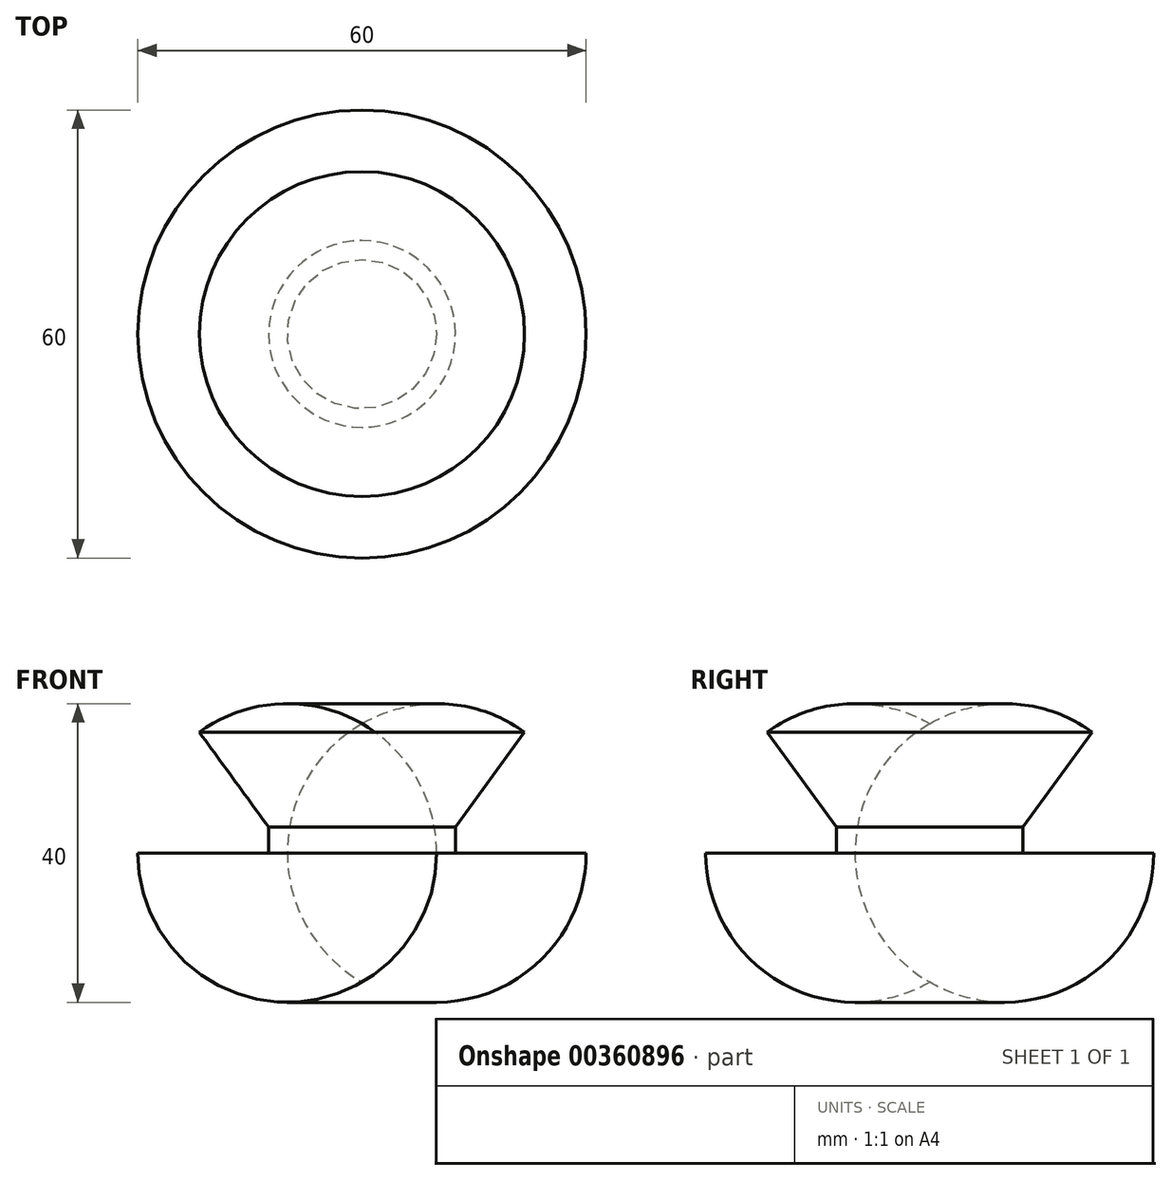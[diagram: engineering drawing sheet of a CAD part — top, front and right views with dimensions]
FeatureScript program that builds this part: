
annotation { "Feature Type Name" : "Feature", "Feature Type Description" : "" }
export const myFeature = defineFeature(function(context is Context, id is Id, definition is map)
    precondition{}
    {
        {
            var Q0;
            Q0=qCreatedBy(makeId("Front.planeOp"),FACE);
            var sketch = newSketch(context, id + "F0", { "sketchPlane" : qUnion([Q0])});
            skLineSegment(sketch, "E0", {"start": v(0, 0) * mm, "end": v(10, 0) * mm});
            skLineSegment(sketch, "E1", {"start": v(0, 0) * mm, "end": v(0, 20) * mm});
            skLineSegment(sketch, "E2", {"start": v(12.5, 3.44) * mm, "end": v(21.76, 16.18) * mm});
            skPoint(sketch, "E3.visualSharp", {"position": v(23.52, 18.6) * mm});
            skLineSegment(sketch, "E4", {"start": v(0, 0) * mm, "end": v(30, 0) * mm});
            skArc(sketch, "E5", {"start": v(30, 0) * mm, "mid": v(27.82, 9.08) * mm, "end": v(21.76, 16.18) * mm});
            skLineSegment(sketch, "E6", {"start": v(10, 0) * mm, "end": v(12.5, 0) * mm});
            skLineSegment(sketch, "E7", {"start": v(12.5, 0) * mm, "end": v(12.5, 3.44) * mm});
            skSolve(sketch);
        }
        {
            var Q0;
            Q0 = qSketchRegion(id + "F0", true);
            var Q1;
            Q1=sQuery(id+"F0.wireOp",EDGE,"E1");
            revolve(context, id + "F1", {"entities" : qUnion([Q0]), "axis" : qUnion([Q1]), "revolveType" : RevolveType.FULL});
        }
    });
